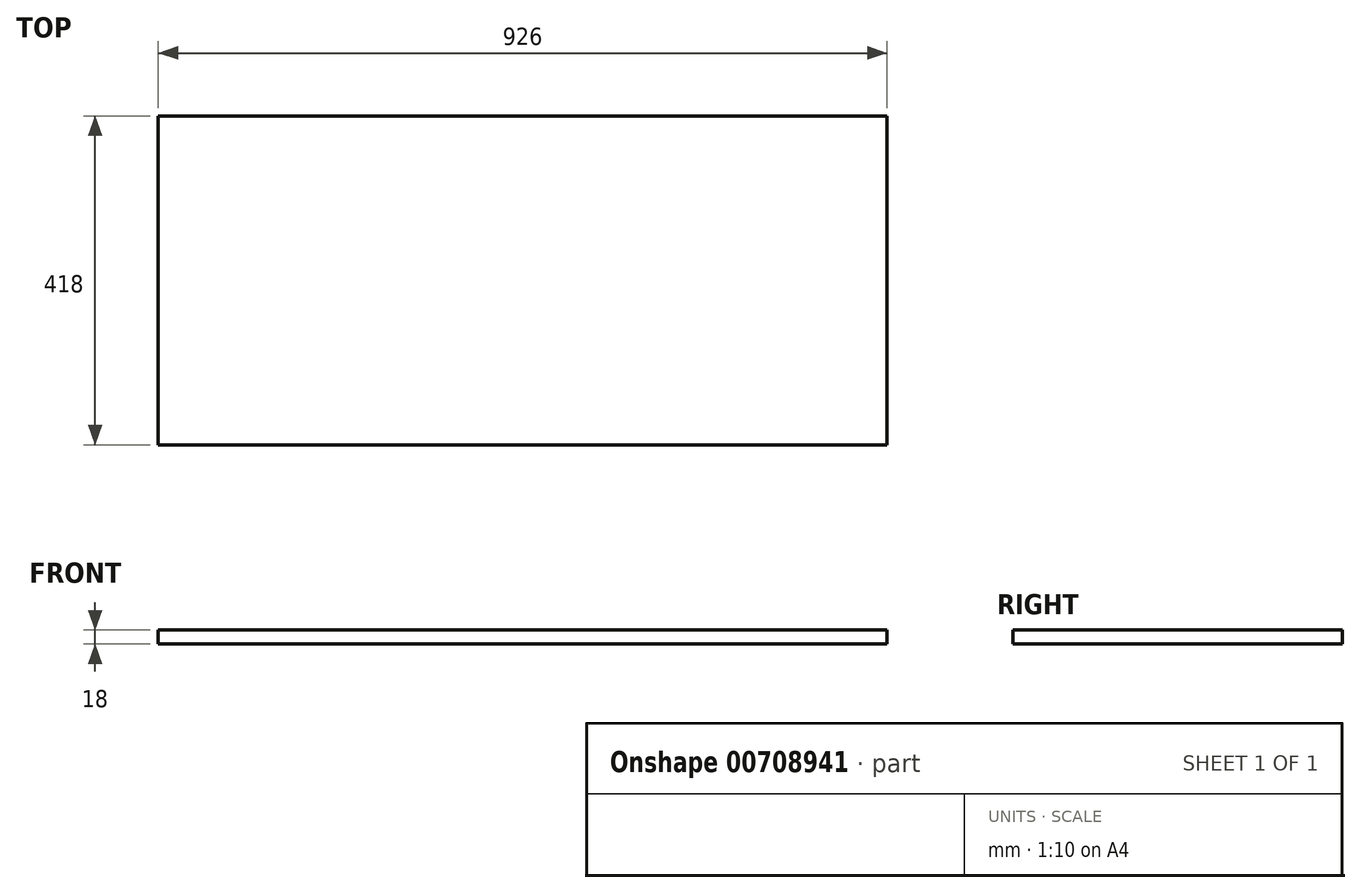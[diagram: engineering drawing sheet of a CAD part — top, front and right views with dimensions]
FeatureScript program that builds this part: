
annotation { "Feature Type Name" : "Feature", "Feature Type Description" : "" }
export const myFeature = defineFeature(function(context is Context, id is Id, definition is map)
    precondition{}
    {
        {
            var Q0;
            Q0=qCreatedBy(makeId("Top.planeOp"),FACE);
            var sketch = newSketch(context, id + "F0", { "sketchPlane" : qUnion([Q0])});
            skLineSegment(sketch, "E0.bottom", {"start": v(0, 0) * mm, "end": v(926, 0) * mm});
            skLineSegment(sketch, "E0.top", {"start": v(0, 418) * mm, "end": v(926, 418) * mm});
            skLineSegment(sketch, "E0.left", {"start": v(0, 0) * mm, "end": v(0, 418) * mm});
            skLineSegment(sketch, "E0.right", {"start": v(926, 0) * mm, "end": v(926, 418) * mm});
            skSolve(sketch);
        }
        {
            var Q0;
            Q0 = qSketchRegion(id + "F0", true);
            extrude(context, id + "F1", {"entities" : qUnion([Q0]), "depth" : 18 * mm, "offsetDistance" : 25 * mm});
        }
    });
